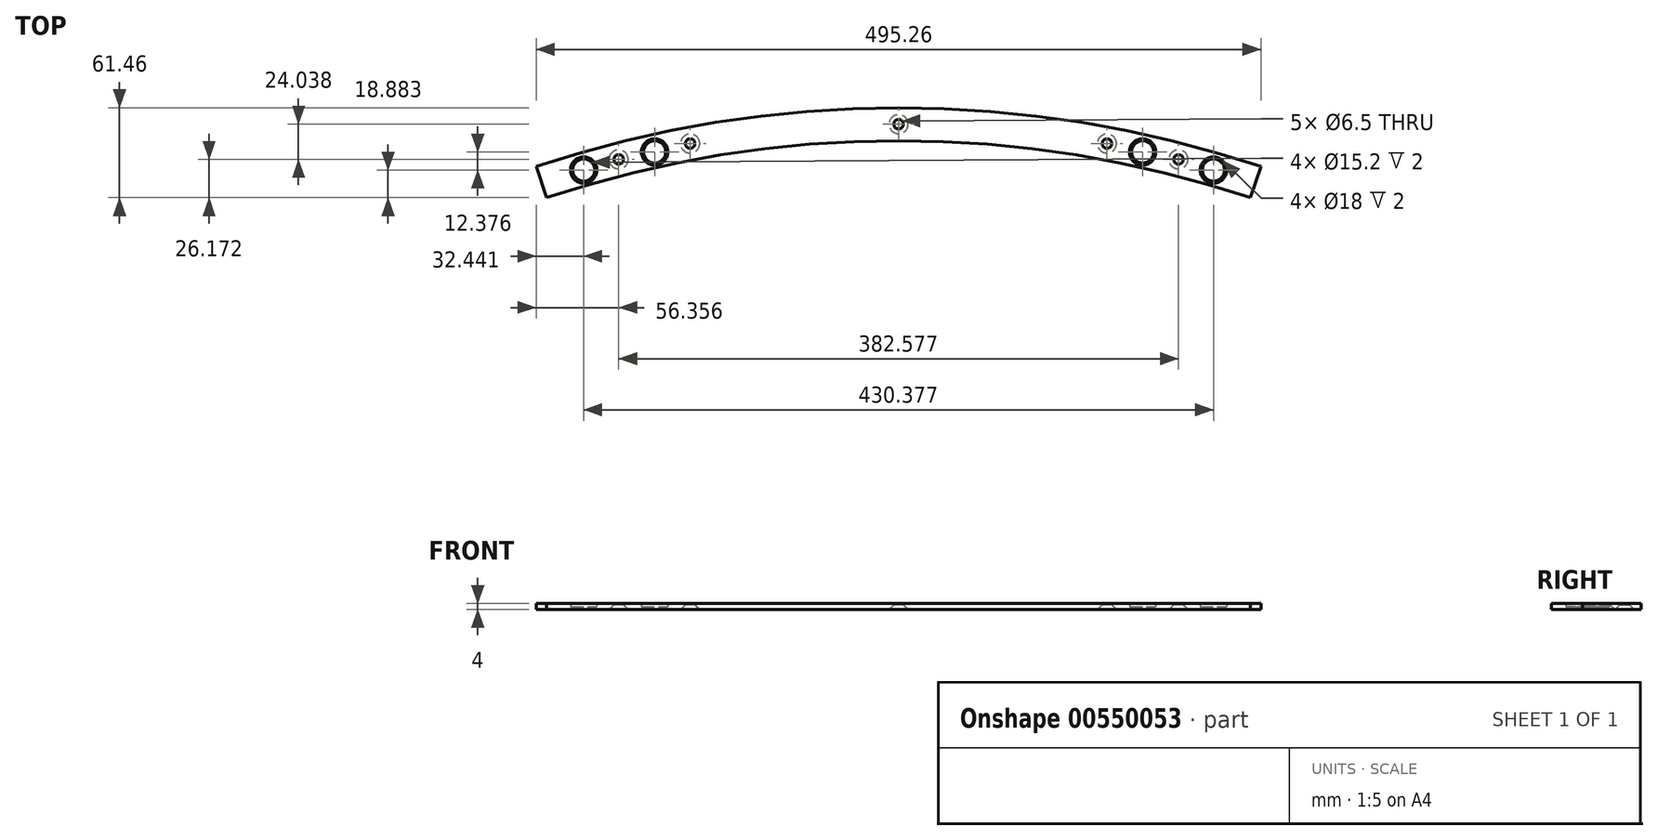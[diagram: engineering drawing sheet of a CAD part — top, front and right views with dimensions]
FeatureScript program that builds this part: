
annotation { "Feature Type Name" : "Feature", "Feature Type Description" : "" }
export const myFeature = defineFeature(function(context is Context, id is Id, definition is map)
    precondition{}
    {
        {
            var Q0;
            Q0=qCreatedBy(makeId("Top.planeOp"),FACE);
            var sketch = newSketch(context, id + "F0", { "sketchPlane" : qUnion([Q0])});
            skLineSegment(sketch, "E0", {"start": v(0, 0) * mm, "end": v(0, 772) * mm, "construction": true});
            skLineSegment(sketch, "E1", {"start": v(0, 0) * mm, "end": v(-243.68, 732.53) * mm, "construction": true});
            skLineSegment(sketch, "E2", {"start": v(0, 0) * mm, "end": v(-167.1, 753.7) * mm, "construction": true});
            skCircle(sketch, "E3", {"center": v(0, 0) * mm, "radius": 772 * mm, "construction": true});
            skPoint(sketch, "E4", {"position": v(-167.1, 753.7) * mm});
            skPoint(sketch, "E5", {"position": v(-243.68, 732.53) * mm});
            skArc(sketch, "E6", {"start": v(-243.68, 732.53) * mm, "mid": v(45.9, 770.63) * mm, "end": v(328.9, 698.44) * mm});
            skSolve(sketch);
        }
        {
            var Q0;
            Q0=qCreatedBy(makeId("Right.planeOp"),FACE);
            var sketch = newSketch(context, id + "F1", { "sketchPlane" : qUnion([Q0])});
            skLineSegment(sketch, "E7", {"start": v(772, 0) * mm, "end": v(762, 0) * mm});
            skLineSegment(sketch, "E8", {"start": v(762, 0) * mm, "end": v(762, 4) * mm});
            skLineSegment(sketch, "E9", {"start": v(762, 4) * mm, "end": v(784.5, 4) * mm});
            skLineSegment(sketch, "E10", {"start": v(772, 0) * mm, "end": v(784.5, 0) * mm});
            skLineSegment(sketch, "E11", {"start": v(784.5, 0) * mm, "end": v(784.5, 4) * mm});
            skLineSegment(sketch, "E12", {"start": v(0, 0) * mm, "end": v(0, 18.51) * mm, "construction": true});
            skLineSegment(sketch, "E13", {"start": v(0, 0) * mm, "end": v(772, 0) * mm, "construction": true});
            skSolve(sketch);
        }
        {
            var Q0;
            Q0=makeQuery(id+"F1.imprint","IMPRINT",FACE,{"disambiguationData":[TD([[makeQuery(id+"F1.imprint","IMPRINT",EDGE,{"derivedFrom":sQuery(id+"F1.wireOp",EDGE,"E7")}),-1.0]])]});
            var Q1;
            Q1=sQuery(id+"F1.wireOp",EDGE,"E12");
            revolve(context, id + "F2", {"surfaceOperationType" : NewSurfaceOperationType.NEW, "entities" : qUnion([Q0]), "axis" : qUnion([Q1]), "revolveType" : RevolveType.SYMMETRIC, "angle" : 36.8 * degree});
        }
        {
            var Q0;
            Q0=makeQuery(id+"F2.opRevolve","SWEPT_FACE",FACE,{"disambiguationData":[OSD([sQuery(id+"F1.wireOp",EDGE,"E7"),sQuery(id+"F1.wireOp",EDGE,"E10")])]});
            var sketch = newSketch(context, id + "F3", { "sketchPlane" : qUnion([Q0])});
            skCircle(sketch, "E14", {"center": v(0, 0) * mm, "radius": 773.25 * mm, "construction": true});
            skPoint(sketch, "E15", {"position": v(-191.27, -749.22) * mm});
            skPoint(sketch, "E16", {"position": v(-142.42, -760.02) * mm});
            skPoint(sketch, "E17", {"position": v(191.3, -749.21) * mm});
            skPoint(sketch, "E18", {"position": v(142.42, -760.02) * mm});
            skLineSegment(sketch, "E19", {"start": v(0, 0) * mm, "end": v(0, -773.25) * mm, "construction": true});
            skPoint(sketch, "E20", {"position": v(0, -773.25) * mm});
            skPoint(sketch, "E21", {"position": v(244.08, -733.72) * mm});
            skLineSegment(sketch, "E22", {"start": v(-240.52, -723.04) * mm, "end": v(-244.08, -733.72) * mm});
            skPoint(sketch, "E23", {"position": v(-244.08, -733.72) * mm});
            skLineSegment(sketch, "E24", {"start": v(-244.08, -733.72) * mm, "end": v(-245.97, -733.09) * mm});
            skSolve(sketch);
        }
        {
            var Q0;
            Q0=sQuery(id+"F3.wireOp",VERTEX,"E16");
            var Q1;
            Q1=sQuery(id+"F3.wireOp",VERTEX,"E15");
            var Q2;
            Q2=sQuery(id+"F3.wireOp",VERTEX,"E18");
            var Q3;
            Q3=sQuery(id+"F3.wireOp",VERTEX,"E17");
            var Q4;
            Q4=sQuery(id+"F3.wireOp",VERTEX,"E20");
            var Q5;
            Q5=makeQuery(id+"F2.opRevolve","SWEPT_BODY",BODY,{"disambiguationData":[OSD([sQuery(id+"F1.wireOp",EDGE,"E7"),sQuery(id+"F1.wireOp",EDGE,"E8"),sQuery(id+"F1.wireOp",EDGE,"E9"),sQuery(id+"F1.wireOp",EDGE,"E10"),sQuery(id+"F1.wireOp",EDGE,"E11")])]});
            hole(context, id + "F4", {"style" : HoleStyle.C_SINK, "endStyle" : HoleEndStyle.THROUGH, "holeDiameter" : 6.5 * mm, "cSinkDiameter" : 13 * mm, "cSinkAngle" : 90 * degree, "majorDiameter" : 5 * mm, "isTappedThrough" : true, "tappedDepth" : 12 * mm, "tapClearance" : 3, "locations" : qUnion([Q0, Q1, Q2, Q3, Q4]), "scope" : qUnion([Q5]), "startStyle" : HoleStartStyle.PART});
        }
        {
            var Q0;
            Q0=makeQuery(id+"F2.opRevolve","SWEPT_FACE",FACE,{"disambiguationData":[OSD([sQuery(id+"F1.wireOp",EDGE,"E9")])]});
            var sketch = newSketch(context, id + "F5", { "sketchPlane" : qUnion([Q0])});
            skPoint(sketch, "E25", {"position": v(-215.19, 741.92) * mm});
            skPoint(sketch, "E26", {"position": v(-166.7, 754.3) * mm});
            skPoint(sketch, "E27", {"position": v(166.76, 754.29) * mm});
            skPoint(sketch, "E28", {"position": v(215.19, 741.92) * mm});
            skSolve(sketch);
        }
        {
            var Q0;
            Q0=sQuery(id+"F5.wireOp",VERTEX,"E25");
            var Q1;
            Q1=sQuery(id+"F5.wireOp",VERTEX,"E26");
            var Q2;
            Q2=sQuery(id+"F5.wireOp",VERTEX,"E28");
            var Q3;
            Q3=sQuery(id+"F5.wireOp",VERTEX,"E27");
            var Q4;
            Q4=makeQuery(id+"F2.opRevolve","SWEPT_BODY",BODY,{"disambiguationData":[OSD([sQuery(id+"F1.wireOp",EDGE,"E7"),sQuery(id+"F1.wireOp",EDGE,"E8"),sQuery(id+"F1.wireOp",EDGE,"E9"),sQuery(id+"F1.wireOp",EDGE,"E10"),sQuery(id+"F1.wireOp",EDGE,"E11")])]});
            hole(context, id + "F6", {"style" : HoleStyle.C_BORE, "endStyle" : HoleEndStyle.THROUGH, "holeDiameter" : 15.2 * mm, "cBoreDiameter" : 18 * mm, "cBoreDepth" : 2 * mm, "majorDiameter" : 5 * mm, "isTappedThrough" : true, "tappedDepth" : 12 * mm, "tapClearance" : 3, "locations" : qUnion([Q0, Q1, Q2, Q3]), "scope" : qUnion([Q4]), "startStyle" : HoleStartStyle.PART});
        }
    });
